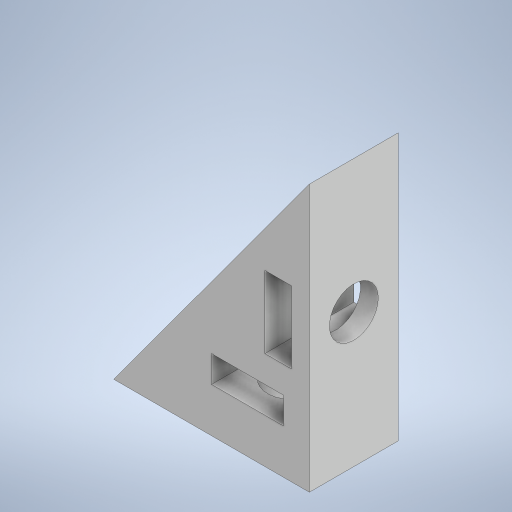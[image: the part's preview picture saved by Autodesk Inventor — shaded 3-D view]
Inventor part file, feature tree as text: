
AUTODESK INVENTOR PART (.ipt)
format: ipt  version: 2023.2 (Build 272271030, 271C)  size: 267,264 bytes
history: native  units: mm
features: extrude x4, sketch x4, projected_geometry x3
ambient origin geometry x8: Origin, YZ Plane, XZ Plane, XY Plane, X Axis, Y Axis, Z Axis, Center Point
bodies: Solid1 (feature_tree)
feature tree (11):
  extrude  "Extrusion1"  Depth=30.0mm
  extrude  "Extrusion2"  Depth=8.1mm
  extrude  "Extrusion3"  Depth=3.0mm
  extrude  "Extrusion4"  Depth=8.1mm
  sketch  "Sketch1"  dims[d0=22.0mm d1=30.0mm]
  sketch  "Sketch2"  dims[d2=10.0mm d3=0.0mm d4=8.1mm]
  projected_geometry  "Projected Loop1"
  sketch  "Sketch3"  dims[d5=5.0mm d6=3.0mm]
  projected_geometry  "Projected Loop2"
  sketch  "Sketch4"  dims[d7=3.0mm d8=8.1mm d9=2.0mm d10=3.0mm d11=0.0mm d12=0.0mm d13=5.5mm d14=10.0mm d15=0.0mm d16=5.5mm d17=10.0mm d18=0.0mm]
  projected_geometry  "Projected Loop3"
